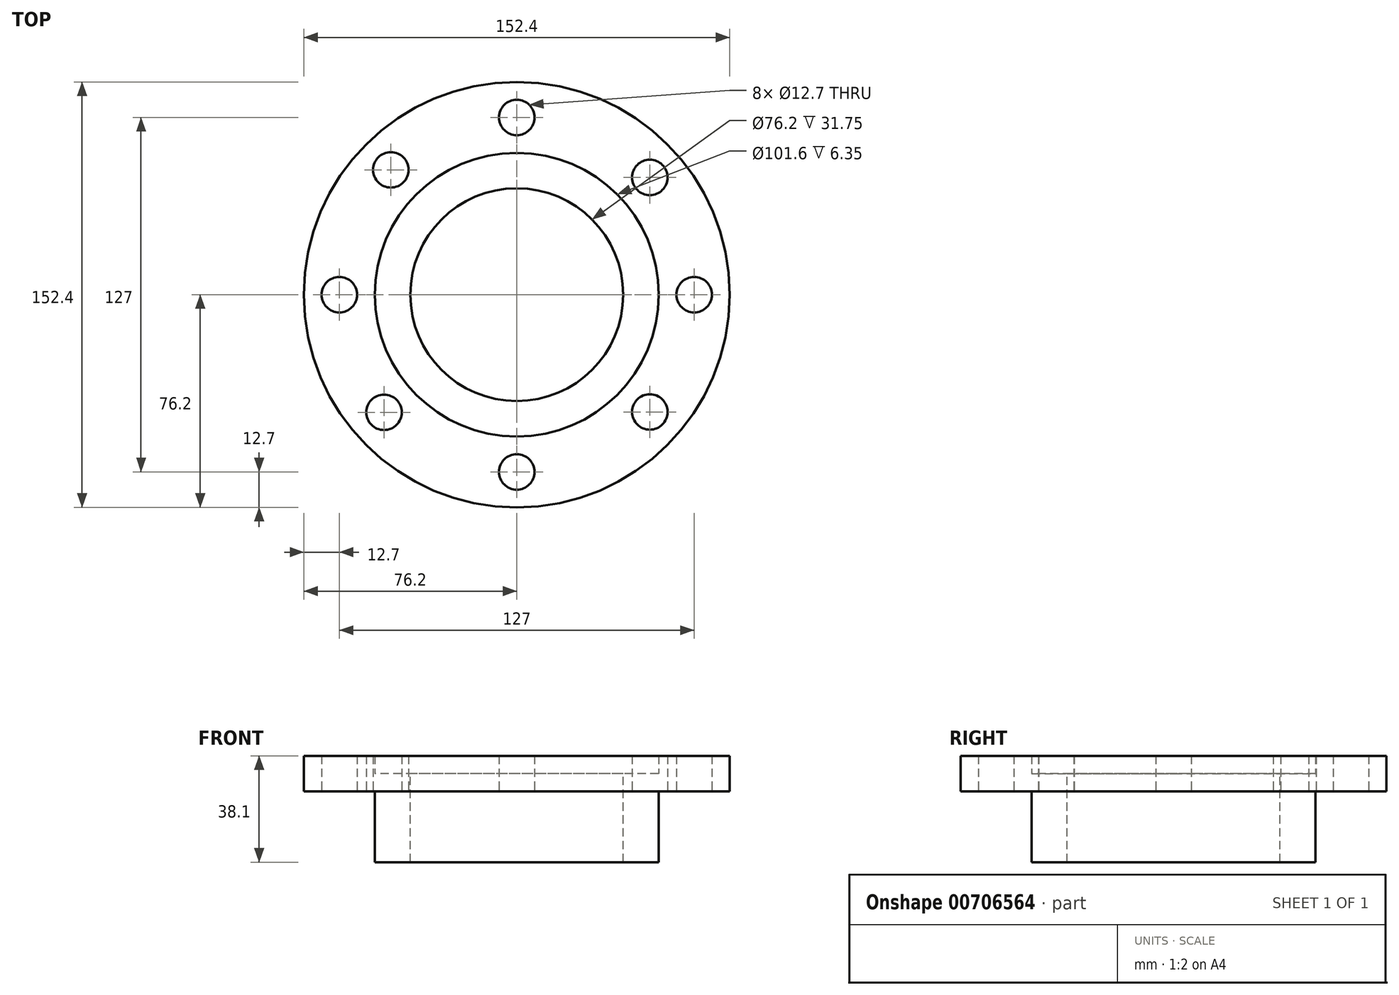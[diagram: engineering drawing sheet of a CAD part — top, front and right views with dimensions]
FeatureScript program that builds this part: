
annotation { "Feature Type Name" : "Feature", "Feature Type Description" : "" }
export const myFeature = defineFeature(function(context is Context, id is Id, definition is map)
    precondition{}
    {
        {
            var Q0;
            Q0=qCreatedBy(makeId("Top.planeOp"),FACE);
            var sketch = newSketch(context, id + "F0", { "sketchPlane" : qUnion([Q0])});
            skCircle(sketch, "E0", {"center": v(0, 0) * mm, "radius": 76.2 * mm});
            skCircle(sketch, "E1", {"center": v(0, 0) * mm, "radius": 50.8 * mm});
            skCircle(sketch, "E2", {"center": v(0, 0) * mm, "radius": 38.1 * mm});
            skLineSegment(sketch, "E3", {"start": v(0, 0) * mm, "end": v(0, 63.5) * mm, "construction": true});
            skCircle(sketch, "E4", {"center": v(0, 63.5) * mm, "radius": 6.35 * mm});
            skCircle(sketch, "E5.MirrorC", {"center": v(0, -63.5) * mm, "radius": 6.35 * mm});
            skCircle(sketch, "E6", {"center": v(0, 0) * mm, "radius": 63.5 * mm, "construction": true});
            skCircle(sketch, "E7", {"center": v(63.5, 0) * mm, "radius": 6.35 * mm});
            skCircle(sketch, "E8", {"center": v(-63.5, 0) * mm, "radius": 6.35 * mm});
            skCircle(sketch, "E9", {"center": v(-45.08, 44.73) * mm, "radius": 6.35 * mm});
            skCircle(sketch, "E10", {"center": v(47.62, 42) * mm, "radius": 6.35 * mm});
            skCircle(sketch, "E11", {"center": v(47.62, -42) * mm, "radius": 6.35 * mm});
            skCircle(sketch, "E12", {"center": v(-47.5, -42.14) * mm, "radius": 6.35 * mm});
            skSolve(sketch);
        }
        {
            var Q0;
            Q0=makeQuery(id+"F0.imprint","IMPRINT",FACE,{"disambiguationData":[TD([[makeQuery(id+"F0.imprint","IMPRINT",EDGE,{"derivedFrom":sQuery(id+"F0.wireOp",EDGE,"E1")}),1.0]])]});
            extrude(context, id + "F1", {"entities" : qUnion([Q0]), "oppositeDirection" : true, "depth" : 31.75 * mm, "offsetDistance" : 25.4 * mm});
        }
        {
            var Q0;
            Q0=makeQuery(id+"F0.imprint","IMPRINT",FACE,{"disambiguationData":[TD([[makeQuery(id+"F0.imprint","IMPRINT",EDGE,{"derivedFrom":sQuery(id+"F0.wireOp",EDGE,"E0")}),1.0]])]});
            extrude(context, id + "F2", {"entities" : qUnion([Q0]), "operationType" : NewBodyOperationType.ADD, "endBound" : BoundingType.SYMMETRIC, "depth" : 12.7 * mm, "offsetDistance" : 25.4 * mm});
        }
    });
